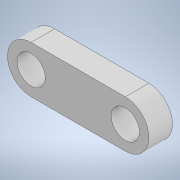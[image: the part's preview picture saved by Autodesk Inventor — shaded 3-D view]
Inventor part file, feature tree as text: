
AUTODESK INVENTOR PART (.ipt)
format: ipt  version: 2022 (Build 260153000, 153)  size: 107,008 bytes
history: native  units: mm
features: extrude x1, sketch x1
ambient origin geometry x8: Origin, YZ Plane, XZ Plane, XY Plane, X Axis, Y Axis, Z Axis, Center Point
bodies: Solid1 (feature_tree)
feature tree (2):
  extrude  "Extrusion1"  Depth=5.0mm
  sketch  "Sketch1"  dims[d0=10.0mm d3=5.0mm d4=0.0mm d5=20.0mm d6=6.0mm]
